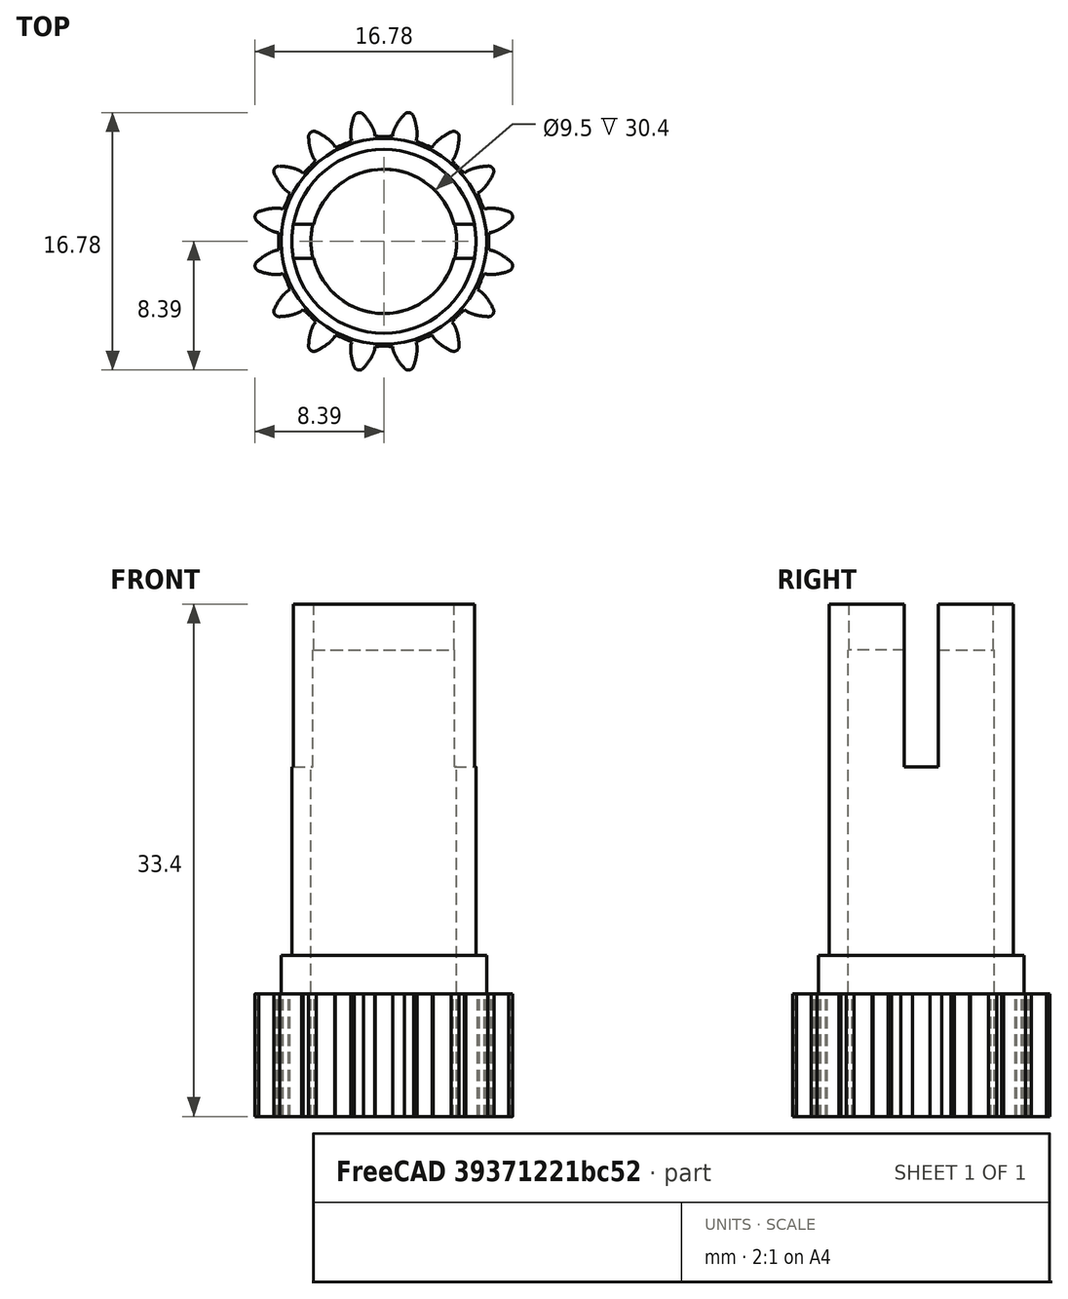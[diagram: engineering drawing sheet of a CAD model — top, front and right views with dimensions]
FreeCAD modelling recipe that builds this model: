
FCSTD DOCUMENT  (FreeCAD 0.17R13522 (Git))
Label: v52_bastago_con_engranaje
License: CreativeCommons Attribution-ShareAlike
LicenseURL: http://creativecommons.org/licenses/by-sa/4.0/
objects: Part::Cut×5, Part::Cylinder×3, Part::Feature×2, Part::Fuse×2, Part::Box×1
note: 13 computed .brp shape members not serialized (recipe doc carries the construction recipe); baked Part::Feature solids carry a one-line shape summary decoded from their .brp

FEATURE [Part::Box] Box  label="hueco aletas"
  AttacherType = Attacher::AttachEngine3D
  Height = 10.7
  Length = 16
  Placement = pos=(-8,-1.1,22.8) rot=(0,0,1;0rad)
  Width = 2.2
FEATURE [Part::Feature] Fusion003001  label="engranaje"
  shape: bbox 16.79 x 16.79 x 30.5 mm, 138 faces (baked)
FEATURE [Part::Cut] Cut  label="engranaje con calces"
  Base = -> Fusion003001
  Refine = true
  Tool = -> Box
FEATURE [Part::Cylinder] Cylinder
  Angle = 360
  AttacherType = Attacher::AttachEngine3D
  Height = 45
  Placement = pos=(0,0,-8) rot=(0,0,1;0rad)
  Radius = 4.75
FEATURE [Part::Cut] Cut001  label="engranaje001"
  Base = -> Cut
  Refine = true
  Tool = -> Cylinder
FEATURE [Part::Cylinder] Cylinder001
  Angle = 360
  AttacherType = Attacher::AttachEngine3D
  Height = 3
  Placement = pos=(0,0,39) rot=(0,0,1;0rad)
  Radius = 4.7
FEATURE [Part::Cylinder] Cylinder002
  Angle = 360
  AttacherType = Attacher::AttachEngine3D
  Height = 3
  Placement = pos=(0,0,39) rot=(0,0,1;0rad)
  Radius = 6
FEATURE [Part::Cut] Cut002
  Base = -> Cylinder002
  Placement = pos=(0,0,-8.6) rot=(0,0,1;0rad)
  Refine = true
  Tool = -> Cylinder001
FEATURE [Part::Cut] Cut003
  Base = -> Cut002
  Refine = true
  Tool = -> Box
FEATURE [Part::Fuse] Fusion
  Base = -> Cut001
  Refine = true
  Tool = -> Cut003
FEATURE [Part::Feature] Cylinder003
  Placement = pos=(0,0,-8) rot=(0,0,1;0rad)
  shape: bbox 9.5 x 9.5 x 45 mm, 3 faces (baked)
FEATURE [Part::Cut] Cut004
  Base = -> Fusion
  Refine = true
  Tool = -> Cylinder003
FEATURE [Part::Fuse] Fusion003002
  Base = -> Cut003
  Refine = true
  Tool = -> Cut004
